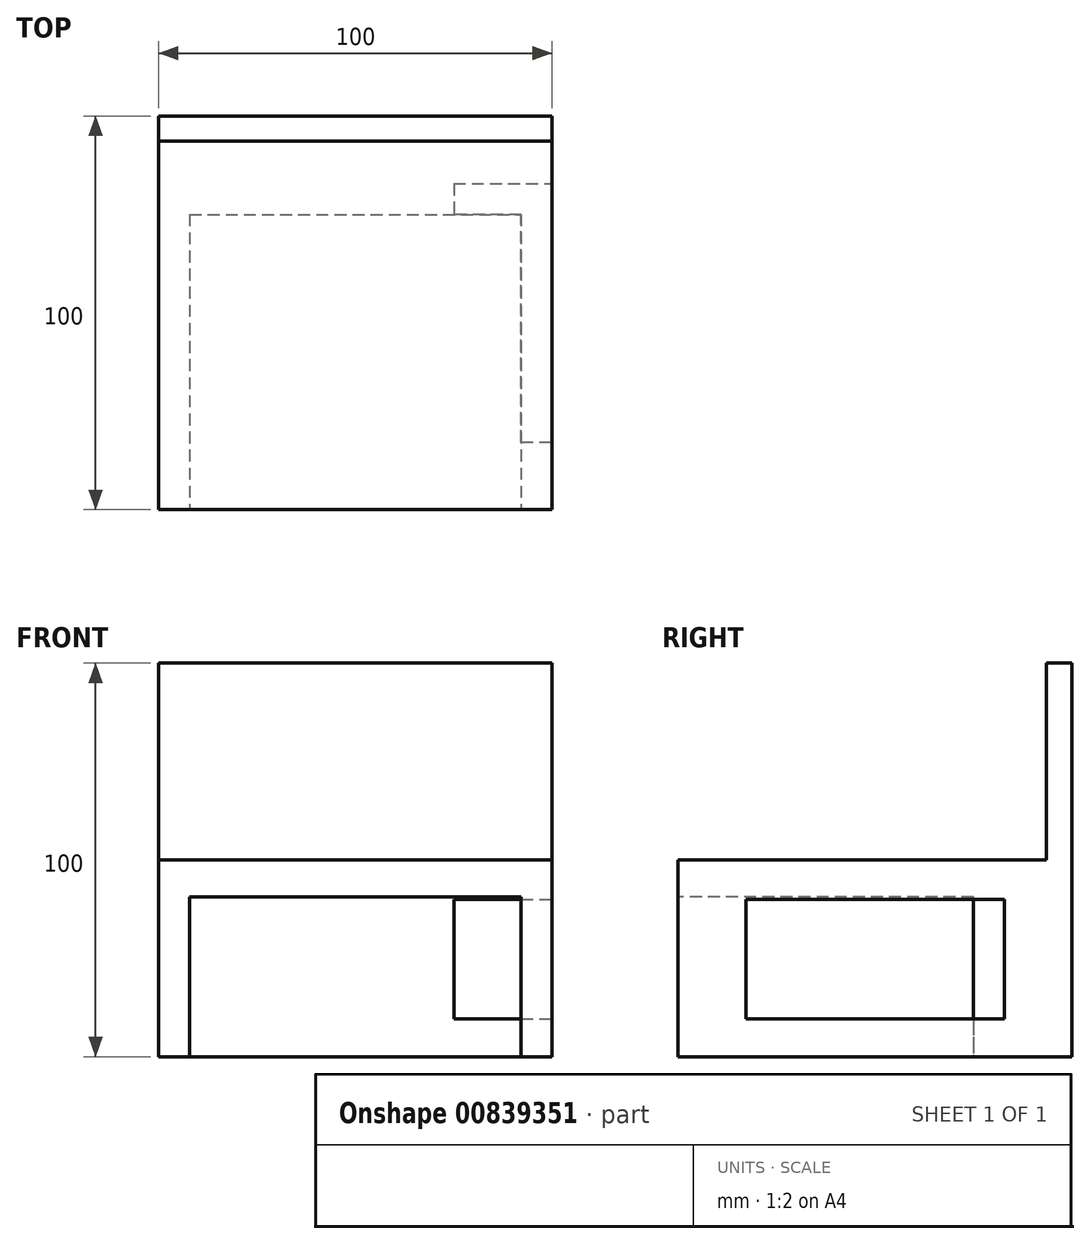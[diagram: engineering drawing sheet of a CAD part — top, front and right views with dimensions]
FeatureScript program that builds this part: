
annotation { "Feature Type Name" : "Feature", "Feature Type Description" : "" }
export const myFeature = defineFeature(function(context is Context, id is Id, definition is map)
    precondition{}
    {
        {
            var Q0;
            Q0=qCreatedBy(makeId("Top.planeOp"),FACE);
            var sketch = newSketch(context, id + "F0", { "sketchPlane" : qUnion([Q0])});
            skLineSegment(sketch, "E0.bottom", {"start": v(-50, 50) * mm, "end": v(50, 50) * mm});
            skLineSegment(sketch, "E0.top", {"start": v(-50, -50) * mm, "end": v(50, -50) * mm});
            skLineSegment(sketch, "E0.left", {"start": v(-50, 50) * mm, "end": v(-50, -50) * mm});
            skLineSegment(sketch, "E0.right", {"start": v(50, 50) * mm, "end": v(50, -50) * mm});
            skPoint(sketch, "E0.middle", {"position": v(0, 0) * mm});
            skSolve(sketch);
        }
        {
            var Q0;
            Q0 = qSketchRegion(id + "F0", true);
            extrude(context, id + "F1", {"entities" : qUnion([Q0]), "depth" : 100 * mm, "offsetDistance" : 25 * mm});
        }
        {
            var Q0;
            Q0=makeQuery(id+"F1.opExtrude","CAP_FACE",FACE,{"disambiguationData":[OSD([sQuery(id+"F0.wireOp",EDGE,"E0.bottom"),sQuery(id+"F0.wireOp",EDGE,"E0.top"),sQuery(id+"F0.wireOp",EDGE,"E0.left"),sQuery(id+"F0.wireOp",EDGE,"E0.right")])],"isStart":false});
            var sketch = newSketch(context, id + "F2", { "sketchPlane" : qUnion([Q0])});
            skLineSegment(sketch, "E1.bottom", {"start": v(50, -50) * mm, "end": v(-50, -50) * mm});
            skLineSegment(sketch, "E1.top", {"start": v(50, 43.6) * mm, "end": v(-50, 43.6) * mm});
            skLineSegment(sketch, "E1.left", {"start": v(50, -50) * mm, "end": v(50, 43.6) * mm});
            skLineSegment(sketch, "E1.right", {"start": v(-50, -50) * mm, "end": v(-50, 43.6) * mm});
            skPoint(sketch, "E1.middle", {"position": v(0, -3.2) * mm});
            skSolve(sketch);
        }
        {
            var Q0;
            Q0 = qSketchRegion(id + "F2", true);
            extrude(context, id + "F3", {"entities" : qUnion([Q0]), "operationType" : NewBodyOperationType.REMOVE, "oppositeDirection" : true, "depth" : 50 * mm, "offsetDistance" : 25 * mm});
        }
        {
            var Q0;
            Q0=makeQuery(id+"F1.opExtrude","SWEPT_FACE",FACE,{"disambiguationData":[OSD([sQuery(id+"F0.wireOp",EDGE,"E0.top")])]});
            var sketch = newSketch(context, id + "F4", { "sketchPlane" : qUnion([Q0])});
            skLineSegment(sketch, "E2.bottom", {"start": v(-42.11, 40.58) * mm, "end": v(42.11, 40.58) * mm});
            skLineSegment(sketch, "E2.top", {"start": v(-42.11, -0.28) * mm, "end": v(42.11, -0.28) * mm});
            skLineSegment(sketch, "E2.left", {"start": v(-42.11, 40.58) * mm, "end": v(-42.11, -0.28) * mm});
            skLineSegment(sketch, "E2.right", {"start": v(42.11, 40.58) * mm, "end": v(42.11, -0.28) * mm});
            skPoint(sketch, "E2.middle", {"position": v(0, 20.15) * mm});
            skSolve(sketch);
        }
        {
            var Q0;
            Q0 = qSketchRegion(id + "F4", true);
            extrude(context, id + "F5", {"entities" : qUnion([Q0]), "operationType" : NewBodyOperationType.REMOVE, "oppositeDirection" : true, "depth" : 75 * mm, "offsetDistance" : 25 * mm});
        }
        {
            var Q0;
            Q0=makeQuery(id+"F1.opExtrude","SWEPT_FACE",FACE,{"disambiguationData":[OSD([sQuery(id+"F0.wireOp",EDGE,"E0.right")])]});
            var sketch = newSketch(context, id + "F6", { "sketchPlane" : qUnion([Q0])});
            skLineSegment(sketch, "E3.bottom", {"start": v(32.82, 9.64) * mm, "end": v(-32.82, 9.64) * mm});
            skLineSegment(sketch, "E3.top", {"start": v(32.82, 39.93) * mm, "end": v(-32.82, 39.93) * mm});
            skLineSegment(sketch, "E3.left", {"start": v(32.82, 9.64) * mm, "end": v(32.82, 39.93) * mm});
            skLineSegment(sketch, "E3.right", {"start": v(-32.82, 9.64) * mm, "end": v(-32.82, 39.93) * mm});
            skPoint(sketch, "E3.middle", {"position": v(0, 24.78) * mm});
            skSolve(sketch);
        }
        {
            var Q0;
            Q0 = qSketchRegion(id + "F6", true);
            extrude(context, id + "F7", {"entities" : qUnion([Q0]), "operationType" : NewBodyOperationType.REMOVE, "oppositeDirection" : true, "depth" : 25 * mm, "offsetDistance" : 25 * mm});
        }
    });
